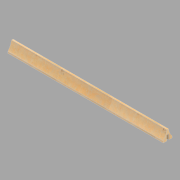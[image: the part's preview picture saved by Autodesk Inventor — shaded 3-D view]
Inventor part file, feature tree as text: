
AUTODESK INVENTOR PART (.ipt)
format: ipt  version: 2022.2 (Build 262287010, 287A)  size: 131,584 bytes
history: native  units: in
note: dims shown in document units (in); Inventor stores cm internally (conversion verified against a paired STEP export)
features: revolve x3, other x1, direct_edit x1
ambient origin geometry x8: Origin, YZ Plane, XZ Plane, XY Plane, X Axis, Y Axis, Z Axis, Center Point
bodies: Solid1 (feature_tree)
feature tree (5):
  other  "Mull"
  direct_edit  "Direct Edit1"
  revolve  "Rotate1"  [1 undecoded]
  revolve  "Rotate2"  Angle=180.0deg
  revolve  "Rotate3"  Angle=180.0deg
note: 1 required parameter value undecoded (feature->parameter linkage not recoverable at this tier; creation-order binding heuristic only, values carry confidence <= 0.55)
